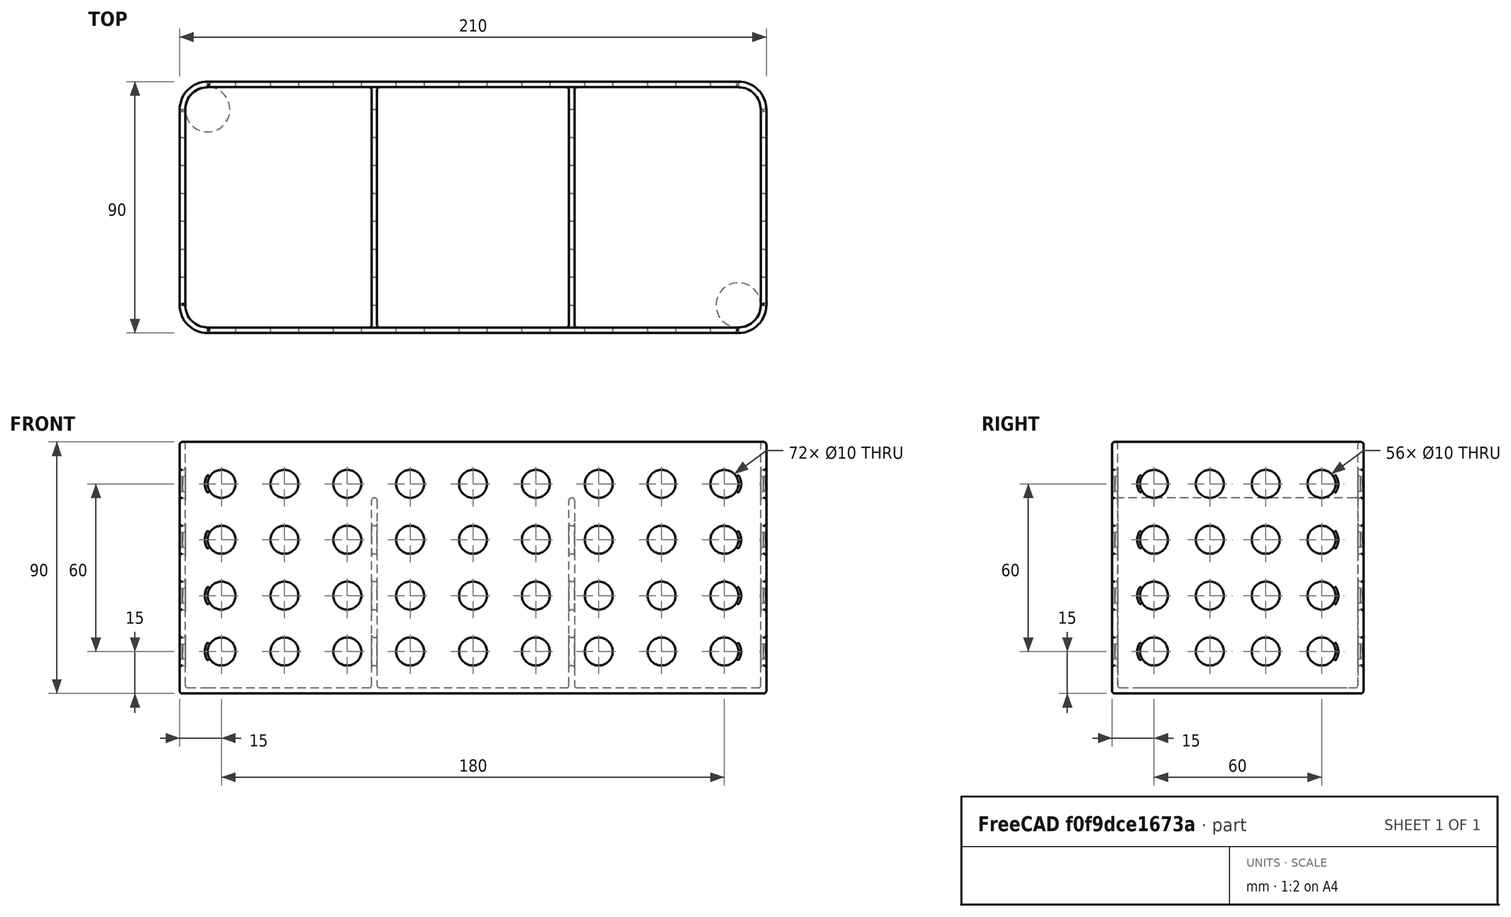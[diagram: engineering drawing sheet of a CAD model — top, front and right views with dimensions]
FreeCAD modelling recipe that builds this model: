
FCSTD DOCUMENT  (FreeCAD 0.21R33040 (Git))
Label: Yet another organizer
License: All rights reserved
LicenseURL: http://en.wikipedia.org/wiki/All_rights_reserved
objects: Sketcher::SketchObject×4, PartDesign::Pad×2, PartDesign::Pocket×2, PartDesign::LinearPattern×2, PartDesign::Thickness×1, PartDesign::Fillet×1, PartDesign::Body×1
note: 19 computed .brp shape members not serialized (recipe doc carries the construction recipe); baked Part::Feature solids carry a one-line shape summary decoded from their .brp

FEATURE [Sketcher::SketchObject] Sketch
  FullyConstrained = true
  MapMode = 5
  Support = -> [XY_Plane]
  sketch-geometry (10):
    g0: ArcOfCircle CenterX=-95 CenterY=35 CenterZ=0 NormalX=0 NormalY=0 NormalZ=1 AngleXU=0 Radius=10 StartAngle=1.5708 EndAngle=3.14159
    g1: LineSegment StartX=-95 StartY=45 StartZ=0 EndX=95 EndY=45 EndZ=0
    g2: ArcOfCircle CenterX=95 CenterY=35 CenterZ=0 NormalX=0 NormalY=0 NormalZ=1 AngleXU=0 Radius=10 StartAngle=1.172e-13 EndAngle=1.5708
    g3: LineSegment StartX=105 StartY=35 StartZ=0 EndX=105 EndY=-35 EndZ=0
    g4: ArcOfCircle CenterX=95 CenterY=-35 CenterZ=0 NormalX=0 NormalY=0 NormalZ=1 AngleXU=0 Radius=10 StartAngle=4.71239 EndAngle=6.28319
    g5: LineSegment StartX=95 StartY=-45 StartZ=0 EndX=-95 EndY=-45 EndZ=0
    g6: ArcOfCircle CenterX=-95 CenterY=-35 CenterZ=0 NormalX=0 NormalY=0 NormalZ=1 AngleXU=0 Radius=10 StartAngle=3.14159 EndAngle=4.71239
    g7: LineSegment StartX=-105 StartY=-35 StartZ=0 EndX=-105 EndY=35 EndZ=0
    g8: GeomPoint X=-105 Y=45 Z=0
    g9: GeomPoint X=105 Y=-45 Z=0
  constraints (23):
    c: Tangent(g0,g1) = 1.5708
    c: Tangent(g1,g2) = 1.5708
    c: Tangent(g2,g3) = 1.5708
    c: Tangent(g3,g4) = 1.5708
    c: Tangent(g4,g5) = 1.5708
    c: Tangent(g5,g6) = 1.5708
    c: Tangent(g6,g7) = 1.5708
    c: Tangent(g7,g0) = 1.5708
    c: Horizontal(g1)
    c: Horizontal(g5)
    c: Vertical(g3)
    c: Vertical(g7)
    c: Equal(g0,g2)
    c: Equal(g2,g4)
    c: Equal(g4,g6)
    c: PointOnObject(g8,g1)
    c: PointOnObject(g8,g7)
    c: PointOnObject(g9,g3)
    c: PointOnObject(g9,g5)
    c: Symmetric(g8,g9,g-1)
    c: Diameter(g0) = 20
    c: DistanceX(g0,g2) = 210
    c: DistanceY(g5,g0) = 90
FEATURE [PartDesign::Pad] Pad
  Direction = (0,0,1)
  Length = 90
  Length2 = 10
  Profile = -> Sketch
  ReferenceAxis = -> Sketch [N_Axis]
  Refine = true
  Type = 0
FEATURE [PartDesign::Thickness] Thickness
  Base = -> Pad [Face10]
  BaseFeature = -> Pad
  Intersection = false
  Join = 0
  Mode = 0
  Refine = true
  Reversed = true
  SupportTransform = false
  Value = 2
FEATURE [Sketcher::SketchObject] Sketch001
  ExternalGeometry = -> [Thickness]
  FullyConstrained = true
  MapMode = 5
  Support = -> [XY_Plane]
  sketch-geometry (11):
    g0: LineSegment StartX=-36.3333 StartY=45 StartZ=0 EndX=-34.3333 EndY=45 EndZ=0
    g1: LineSegment StartX=-34.3333 StartY=45 StartZ=0 EndX=-34.3333 EndY=-45 EndZ=0
    g2: LineSegment StartX=-34.3333 StartY=-45 StartZ=0 EndX=-36.3333 EndY=-45 EndZ=0
    g3: LineSegment StartX=-36.3333 StartY=-45 StartZ=0 EndX=-36.3333 EndY=45 EndZ=0
    g4: LineSegment StartX=34.3333 StartY=45 StartZ=0 EndX=36.3333 EndY=45 EndZ=0
    g5: LineSegment StartX=36.3333 StartY=45 StartZ=0 EndX=36.3333 EndY=-45 EndZ=0
    g6: LineSegment StartX=36.3333 StartY=-45 StartZ=0 EndX=34.3333 EndY=-45 EndZ=0
    g7: LineSegment StartX=34.3333 StartY=-45 StartZ=0 EndX=34.3333 EndY=45 EndZ=0
    g8: LineSegment StartX=-105 StartY=35 StartZ=0 EndX=-36.3333 EndY=35 EndZ=0
    g9: LineSegment StartX=-34.3333 StartY=35 StartZ=0 EndX=34.3333 EndY=35 EndZ=0
    g10: LineSegment StartX=36.3333 StartY=35 StartZ=0 EndX=105 EndY=35 EndZ=0
  constraints (34):
    c: Coincident(g0,g1)
    c: Coincident(g1,g2)
    c: Coincident(g2,g3)
    c: Coincident(g3,g0)
    c: Horizontal(g0)
    c: Horizontal(g2)
    c: Vertical(g1)
    c: Vertical(g3)
    c: PointOnObject(g0,g-3)
    c: PointOnObject(g1,g-4)
    c: DistanceX(g2,g2) = 2
    c: Coincident(g4,g5)
    c: Coincident(g5,g6)
    c: Coincident(g6,g7)
    c: Coincident(g7,g4)
    c: Horizontal(g4)
    c: Horizontal(g6)
    c: Vertical(g5)
    c: Vertical(g7)
    c: PointOnObject(g4,g-3)
    c: PointOnObject(g5,g-4)
    c: Equal(g2,g6)
    c: Coincident(g8,g-5)
    c: PointOnObject(g8,g3)
    c: Horizontal(g8)
    c: PointOnObject(g9,g1)
    c: PointOnObject(g9,g7)
    c: Horizontal(g9)
    c: PointOnObject(g10,g5)
    c: Coincident(g10,g-6)
    c: Horizontal(g10)
    c: Horizontal(g9,g8)
    c: Equal(g8,g9)
    c: Equal(g10,g9)
FEATURE [PartDesign::Pad] Pad001
  BaseFeature = -> Thickness
  Direction = (0,0,1)
  Length = 70
  Length2 = 10
  Profile = -> Sketch001
  ReferenceAxis = -> Sketch001 [N_Axis]
  Refine = true
  Type = 0
FEATURE [Sketcher::SketchObject] Sketch002
  FullyConstrained = true
  MapMode = 5
  Placement = pos=(0,0,0) rot=(1,0,0;1.5708rad)
  Support = -> [XZ_Plane]
  sketch-geometry (7):
    g0: Circle CenterX=-90 CenterY=75 CenterZ=0 NormalX=0 NormalY=0 NormalZ=1 AngleXU=0 Radius=5
    g1: Circle CenterX=-90 CenterY=55 CenterZ=0 NormalX=0 NormalY=0 NormalZ=1 AngleXU=0 Radius=5
    g2: Circle CenterX=-90 CenterY=35 CenterZ=0 NormalX=0 NormalY=0 NormalZ=1 AngleXU=0 Radius=5
    g3: Circle CenterX=-90 CenterY=15 CenterZ=0 NormalX=0 NormalY=0 NormalZ=1 AngleXU=0 Radius=5
    g4: LineSegment StartX=-90 StartY=75 StartZ=0 EndX=-90 EndY=55 EndZ=0
    g5: LineSegment StartX=-90 StartY=55 StartZ=0 EndX=-90 EndY=35 EndZ=0
    g6: LineSegment StartX=-90 StartY=35 StartZ=0 EndX=-90 EndY=15 EndZ=0
  constraints (18):
    c: Diameter(g0) = 10
    c: Equal(g0,g1)
    c: Equal(g1,g2)
    c: Equal(g2,g3)
    c: Vertical(g1,g0)
    c: Vertical(g0,g2)
    c: Vertical(g2,g3)
    c: Coincident(g4,g0)
    c: Coincident(g4,g1)
    c: Coincident(g5,g1)
    c: Coincident(g5,g2)
    c: Coincident(g6,g2)
    c: Coincident(g6,g3)
    c: Equal(g4,g5)
    c: Equal(g5,g6)
    c: DistanceY(g3) = 15
    c: DistanceX(g3,g-1) = 90
    c: DistanceY(g4,g4) = 20
FEATURE [PartDesign::Pocket] Pocket
  BaseFeature = -> Pad001
  Direction = (0,1,2e-16)
  Length = 5
  Length2 = 5
  Midplane = true
  Profile = -> Sketch002
  ReferenceAxis = -> Sketch002 [N_Axis]
  Refine = true
  Type = 1
FEATURE [PartDesign::LinearPattern] LinearPattern
  BaseFeature = -> Pocket
  Direction = -> Sketch002 [H_Axis]
  Length = 180
  Occurrences = 9
  Originals = -> [Pocket]
  Refine = true
FEATURE [Sketcher::SketchObject] Sketch003
  FullyConstrained = true
  MapMode = 5
  Placement = pos=(0,0,0) rot=(0.57735,0.57735,0.57735;2.0944rad)
  Support = -> [YZ_Plane]
  sketch-geometry (7):
    g0: Circle CenterX=-30 CenterY=15 CenterZ=0 NormalX=0 NormalY=0 NormalZ=1 AngleXU=0 Radius=5
    g1: Circle CenterX=-30 CenterY=35 CenterZ=0 NormalX=0 NormalY=0 NormalZ=1 AngleXU=0 Radius=5
    g2: Circle CenterX=-30 CenterY=55 CenterZ=0 NormalX=0 NormalY=0 NormalZ=1 AngleXU=0 Radius=5
    g3: Circle CenterX=-30 CenterY=75 CenterZ=0 NormalX=0 NormalY=0 NormalZ=1 AngleXU=0 Radius=5
    g4: LineSegment StartX=-30 StartY=75 StartZ=0 EndX=-30 EndY=55 EndZ=0
    g5: LineSegment StartX=-30 StartY=55 StartZ=0 EndX=-30 EndY=35 EndZ=0
    g6: LineSegment StartX=-30 StartY=35 StartZ=0 EndX=-30 EndY=15 EndZ=0
  constraints (18):
    c: Equal(g3,g2)
    c: Equal(g2,g1)
    c: Equal(g1,g0)
    c: Diameter(g3) = 10
    c: Coincident(g4,g3)
    c: Coincident(g4,g2)
    c: Coincident(g5,g2)
    c: Coincident(g5,g1)
    c: Coincident(g6,g1)
    c: Coincident(g6,g0)
    c: Vertical(g6)
    c: Vertical(g5)
    c: Vertical(g4)
    c: Equal(g6,g5)
    c: Equal(g5,g4)
    c: DistanceY(g0) = 15
    c: DistanceY(g6,g6) = 20
    c: DistanceX(g0,g-1) = 30
FEATURE [PartDesign::Pocket] Pocket001
  BaseFeature = -> LinearPattern
  Direction = (-1,2e-16,-3e-16)
  Length = 5
  Length2 = 5
  Midplane = true
  Profile = -> Sketch003
  ReferenceAxis = -> Sketch003 [N_Axis]
  Refine = true
  Type = 1
FEATURE [PartDesign::LinearPattern] LinearPattern001
  BaseFeature = -> Pocket001
  Direction = -> Sketch003 [H_Axis]
  Length = 60
  Occurrences = 4
  Originals = -> [Pocket001]
  Refine = true
FEATURE [PartDesign::Fillet] Fillet
  Base = -> LinearPattern001 [Face62,Face60,Face2,Face3,Face64,Face70,Face68,Face66,Face127,Face128,Face124,Face125]
  BaseFeature = -> LinearPattern001
  Radius = 0.9
  Refine = true
  SupportTransform = false
  UseAllEdges = false
FEATURE [PartDesign::Body] Body
  Group = -> [Sketch,Pad,Thickness,Sketch001,Pad001,Sketch002,Pocket,LinearPattern,Sketch003,Pocket001,LinearPattern001,Fillet]
  Origin = -> Origin
  Tip = -> Fillet
